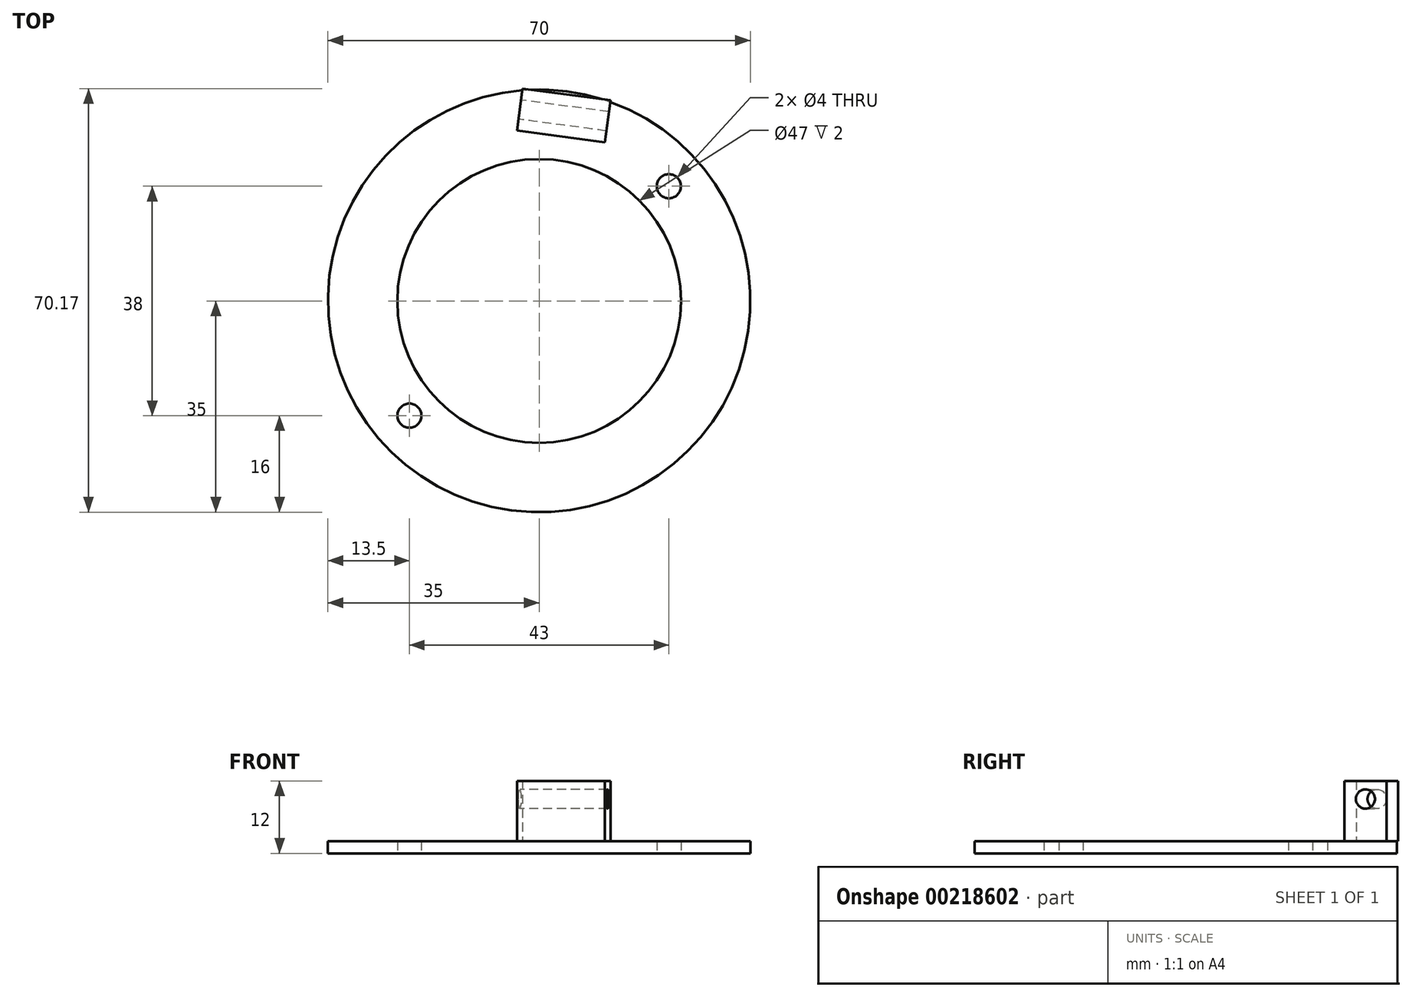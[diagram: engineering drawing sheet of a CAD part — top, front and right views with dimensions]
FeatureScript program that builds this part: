
annotation { "Feature Type Name" : "Feature", "Feature Type Description" : "" }
export const myFeature = defineFeature(function(context is Context, id is Id, definition is map)
    precondition{}
    {
        {
            var Q0;
            Q0=qCreatedBy(makeId("Top.planeOp"),FACE);
            var sketch = newSketch(context, id + "F0", { "sketchPlane" : qUnion([Q0])});
            skCircle(sketch, "E0", {"center": v(0, 0) * mm, "radius": 35 * mm});
            skCircle(sketch, "E1", {"center": v(0, 0) * mm, "radius": 23.5 * mm});
            skSolve(sketch);
        }
        {
            var Q0;
            Q0 = qSketchRegion(id + "F0", true);
            extrude(context, id + "F1", {"entities" : qUnion([Q0]), "depth" : 2 * mm, "offsetDistance" : 25 * mm});
        }
        {
            var Q0;
            Q0=qCreatedBy(makeId("Top.planeOp"),FACE);
            var sketch = newSketch(context, id + "F2", { "sketchPlane" : qUnion([Q0])});
            skCircle(sketch, "E2", {"center": v(-21.5, -19) * mm, "radius": 2 * mm});
            skCircle(sketch, "E3", {"center": v(21.5, 19) * mm, "radius": 2 * mm});
            skLineSegment(sketch, "E4", {"start": v(57.6, 0) * mm, "end": v(0, 0) * mm, "construction": true});
            skLineSegment(sketch, "E5", {"start": v(0, 0) * mm, "end": v(0, 40.1) * mm, "construction": true});
            skSolve(sketch);
        }
        {
            var Q0;
            Q0 = qSketchRegion(id + "F2", true);
            extrude(context, id + "F3", {"entities" : qUnion([Q0]), "operationType" : NewBodyOperationType.REMOVE, "endBound" : BoundingType.THROUGH_ALL, "depth" : 25 * mm, "offsetDistance" : 25 * mm});
        }
        {
            var Q0;
            Q0=makeQuery(id+"F1.opExtrude","CAP_FACE",FACE,{"disambiguationData":[OSD([sQuery(id+"F0.wireOp",EDGE,"E0"),sQuery(id+"F0.wireOp",EDGE,"E1")])],"isStart":false});
            var sketch = newSketch(context, id + "F4", { "sketchPlane" : qUnion([Q0])});
            skLineSegment(sketch, "E6", {"start": v(-2.76, 35.17) * mm, "end": v(-3.68, 28.23) * mm});
            skLineSegment(sketch, "E7", {"start": v(-3.68, 28.23) * mm, "end": v(10.9, 26.3) * mm});
            skLineSegment(sketch, "E8", {"start": v(10.9, 26.3) * mm, "end": v(11.8, 33.24) * mm});
            skLineSegment(sketch, "E9", {"start": v(11.8, 33.24) * mm, "end": v(-2.76, 35.17) * mm});
            skLineSegment(sketch, "E10", {"start": v(-21.5, -19) * mm, "end": v(21.5, 19) * mm, "construction": true});
            skLineSegment(sketch, "E11", {"start": v(0, 0) * mm, "end": v(3.6, 27.26) * mm, "construction": true});
            skSolve(sketch);
        }
        {
            var Q0;
            Q0 = qSketchRegion(id + "F4", true);
            extrude(context, id + "F5", {"entities" : qUnion([Q0]), "operationType" : NewBodyOperationType.ADD, "depth" : 10 * mm, "offsetDistance" : 25 * mm});
        }
        {
            var Q0;
            Q0=makeQuery(id+"F5.opExtrude","SWEPT_FACE",FACE,{"disambiguationData":[OSD([sQuery(id+"F4.wireOp",EDGE,"E6")])]});
            var sketch = newSketch(context, id + "F6", { "sketchPlane" : qUnion([Q0])});
            skCircle(sketch, "E12", {"center": v(-31, 9) * mm, "radius": 1.6 * mm});
            skPoint(sketch, "E12.centerSnap0", {"position": v(-31, 12) * mm});
            skSolve(sketch);
        }
        {
            var Q0;
            Q0 = qSketchRegion(id + "F6", true);
            extrude(context, id + "F7", {"entities" : qUnion([Q0]), "operationType" : NewBodyOperationType.REMOVE, "endBound" : BoundingType.THROUGH_ALL, "oppositeDirection" : true, "depth" : 25 * mm, "offsetDistance" : 25 * mm});
        }
    });
